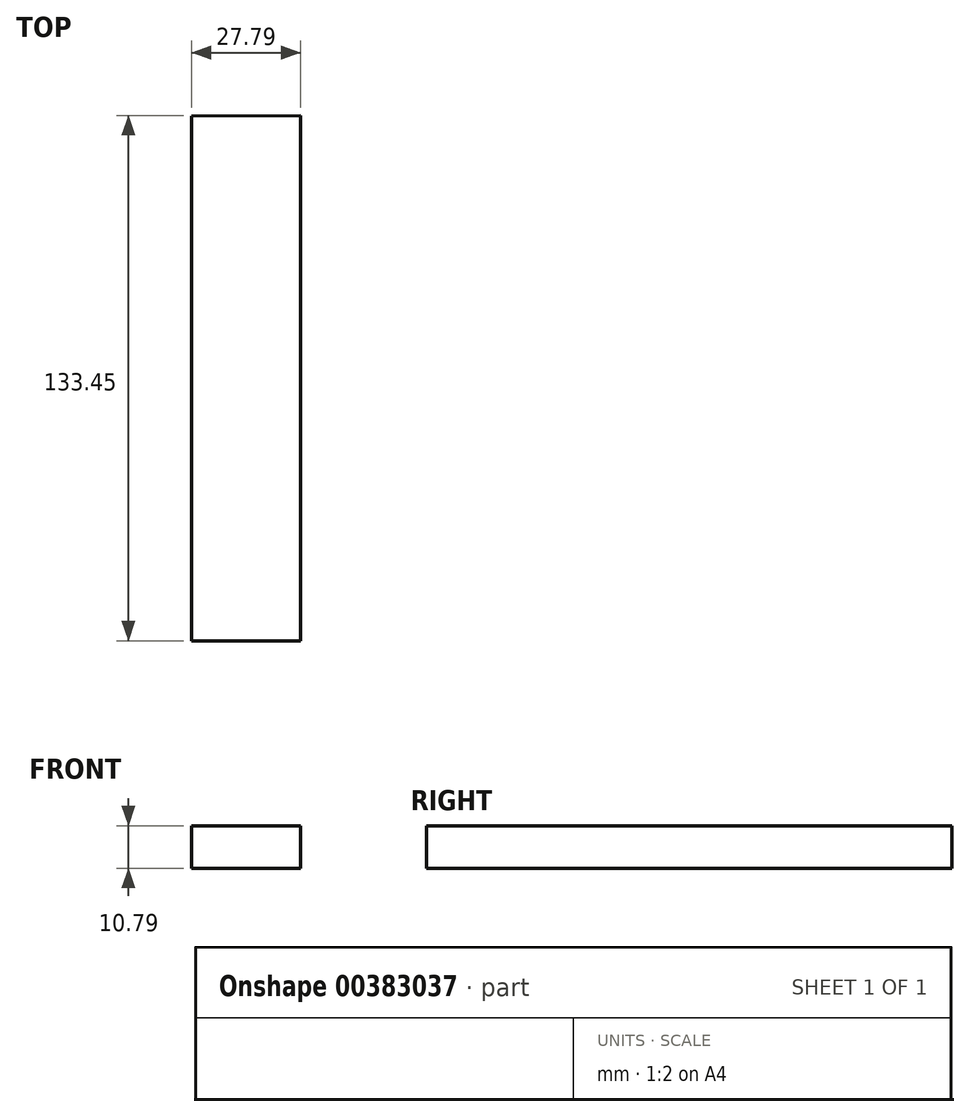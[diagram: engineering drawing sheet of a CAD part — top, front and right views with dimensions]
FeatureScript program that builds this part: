
annotation { "Feature Type Name" : "Feature", "Feature Type Description" : "" }
export const myFeature = defineFeature(function(context is Context, id is Id, definition is map)
    precondition{}
    {
        {
            var Q0;
            Q0=qCreatedBy(makeId("Top.planeOp"),FACE);
            var sketch = newSketch(context, id + "F0", { "sketchPlane" : qUnion([Q0])});
            skLineSegment(sketch, "E0", {"start": v(0, 68.5) * mm, "end": v(0, -64.95) * mm});
            skLineSegment(sketch, "E1", {"start": v(0, -64.95) * mm, "end": v(-27.8, -64.95) * mm});
            skLineSegment(sketch, "E2", {"start": v(-27.8, -64.95) * mm, "end": v(-27.8, 68.43) * mm});
            skLineSegment(sketch, "E3", {"start": v(-27.8, 68.43) * mm, "end": v(0, 68.5) * mm});
            skSolve(sketch);
        }
        {
            var Q0;
            Q0=makeQuery(id+"F0.imprint","IMPRINT",FACE,{"disambiguationData":[TD([[makeQuery(id+"F0.imprint","IMPRINT",EDGE,{"derivedFrom":sQuery(id+"F0.wireOp",EDGE,"E0")}),-1.0]])]});
            extrude(context, id + "F1", {"entities" : qUnion([Q0]), "depth" : 10.8 * mm});
        }
    });
